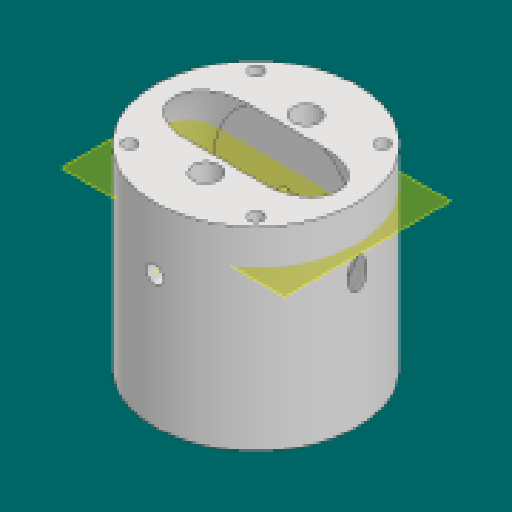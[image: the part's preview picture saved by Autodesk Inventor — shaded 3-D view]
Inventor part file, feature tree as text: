
AUTODESK INVENTOR PART (.ipt)
format: ipt  version: 2023.1 (Build 271208000, 208)  size: 196,608 bytes
history: native  units: in
note: dims shown in document units (in); Inventor stores cm internally (conversion verified against a paired STEP export)
features: sketch x3, extrude x2, revolve x1, other x1, plane x1
ambient origin geometry x8: Origin, YZ Plane, XZ Plane, XY Plane, X Axis, Y Axis, Z Axis, Center Point
bodies: Solid1 (feature_tree)
feature tree (8):
  extrude  "Extrusion1"  Depth=0.1875in
  revolve  "Revolution1"  Angle=45.0deg
  other  "Work Axis3"
  extrude  "Extrusion3"  Depth=0.375in
  plane  "Work Plane2"
  sketch  "Sketch1"  dims[d1=0.1875in d2=0.5in]
  sketch  "Sketch3"  dims[d3=0.0787in d4=45.0deg]
  sketch  "Sketch6"  dims[d5=1.5748in d7=360.0deg d10=0.375in d11=2.75in d12=0.0in d22=2.75in d23=0.1575in d24=2.25in d26=360.0deg d29=0.4331in d37=2.75in d38=0.125in d39=0.125in d40=0.0in d41=0.0in d42=0.5in d49=-0.5in d53=0.75in d54=0.5in d55=2.8346in]
